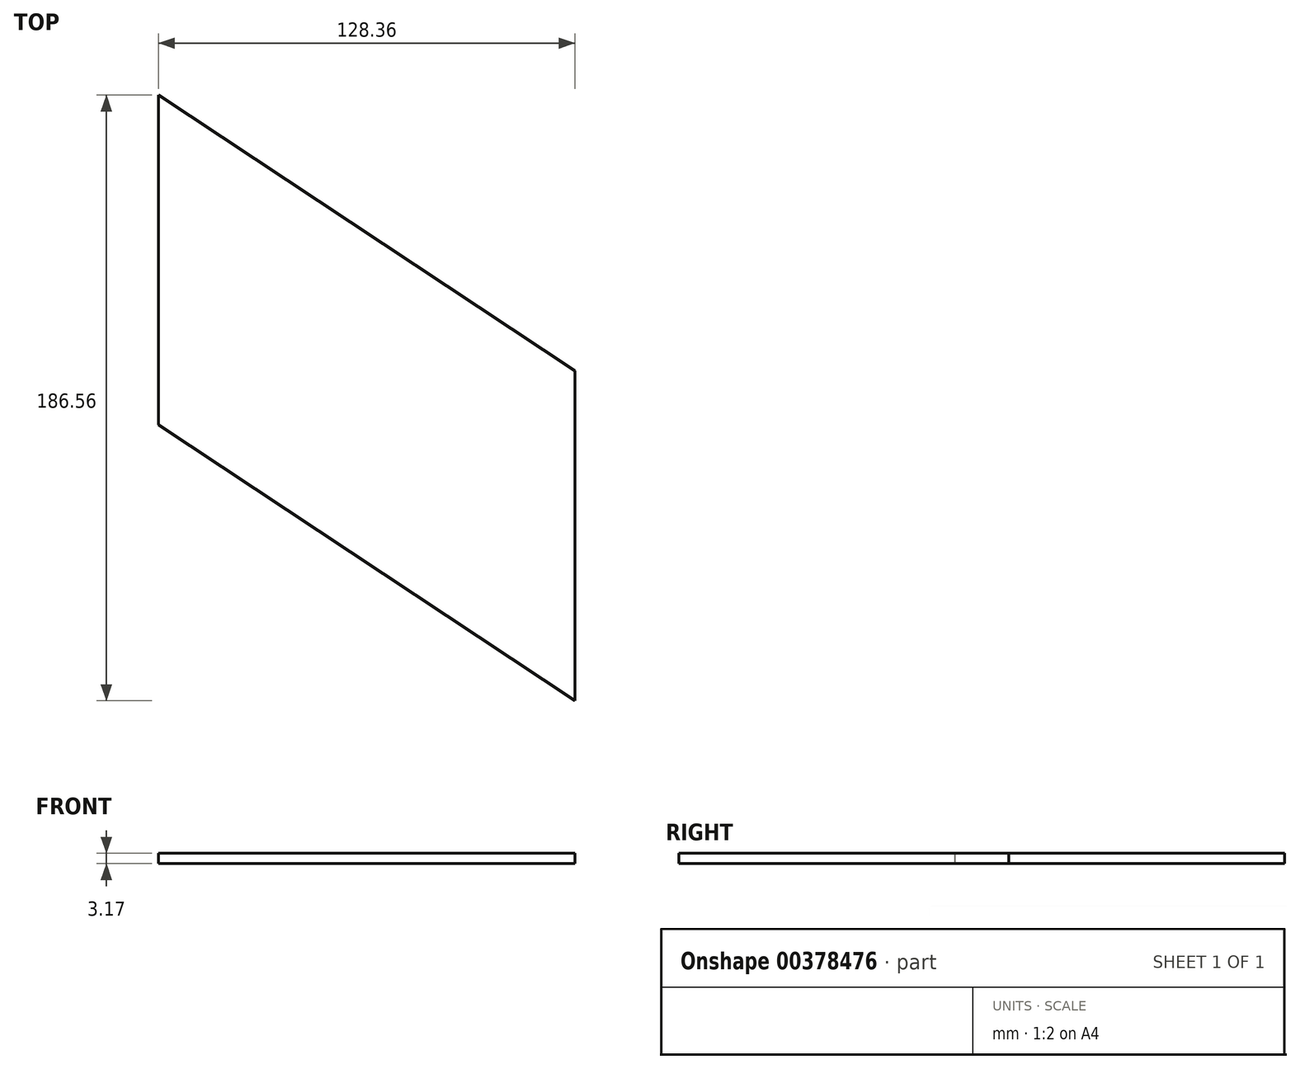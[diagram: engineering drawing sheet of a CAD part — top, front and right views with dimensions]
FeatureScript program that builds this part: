
annotation { "Feature Type Name" : "Feature", "Feature Type Description" : "" }
export const myFeature = defineFeature(function(context is Context, id is Id, definition is map)
    precondition{}
    {
        {
            var Q0;
            Q0=qCreatedBy(makeId("Top.planeOp"),FACE);
            var sketch = newSketch(context, id + "F0", { "sketchPlane" : qUnion([Q0])});
            skLineSegment(sketch, "E0", {"start": v(0, 0) * mm, "end": v(0, 101.6) * mm});
            skLineSegment(sketch, "E1", {"start": v(0, 101.6) * mm, "end": v(-128.36, 186.56) * mm});
            skLineSegment(sketch, "E2", {"start": v(-128.36, 186.56) * mm, "end": v(-128.36, 84.96) * mm});
            skLineSegment(sketch, "E3", {"start": v(-128.36, 84.96) * mm, "end": v(0, 0) * mm});
            skSolve(sketch);
        }
        {
            var Q0;
            Q0 = qSketchRegion(id + "F0", true);
            extrude(context, id + "F1", {"entities" : qUnion([Q0]), "depth" : 3.17 * mm});
        }
    });
